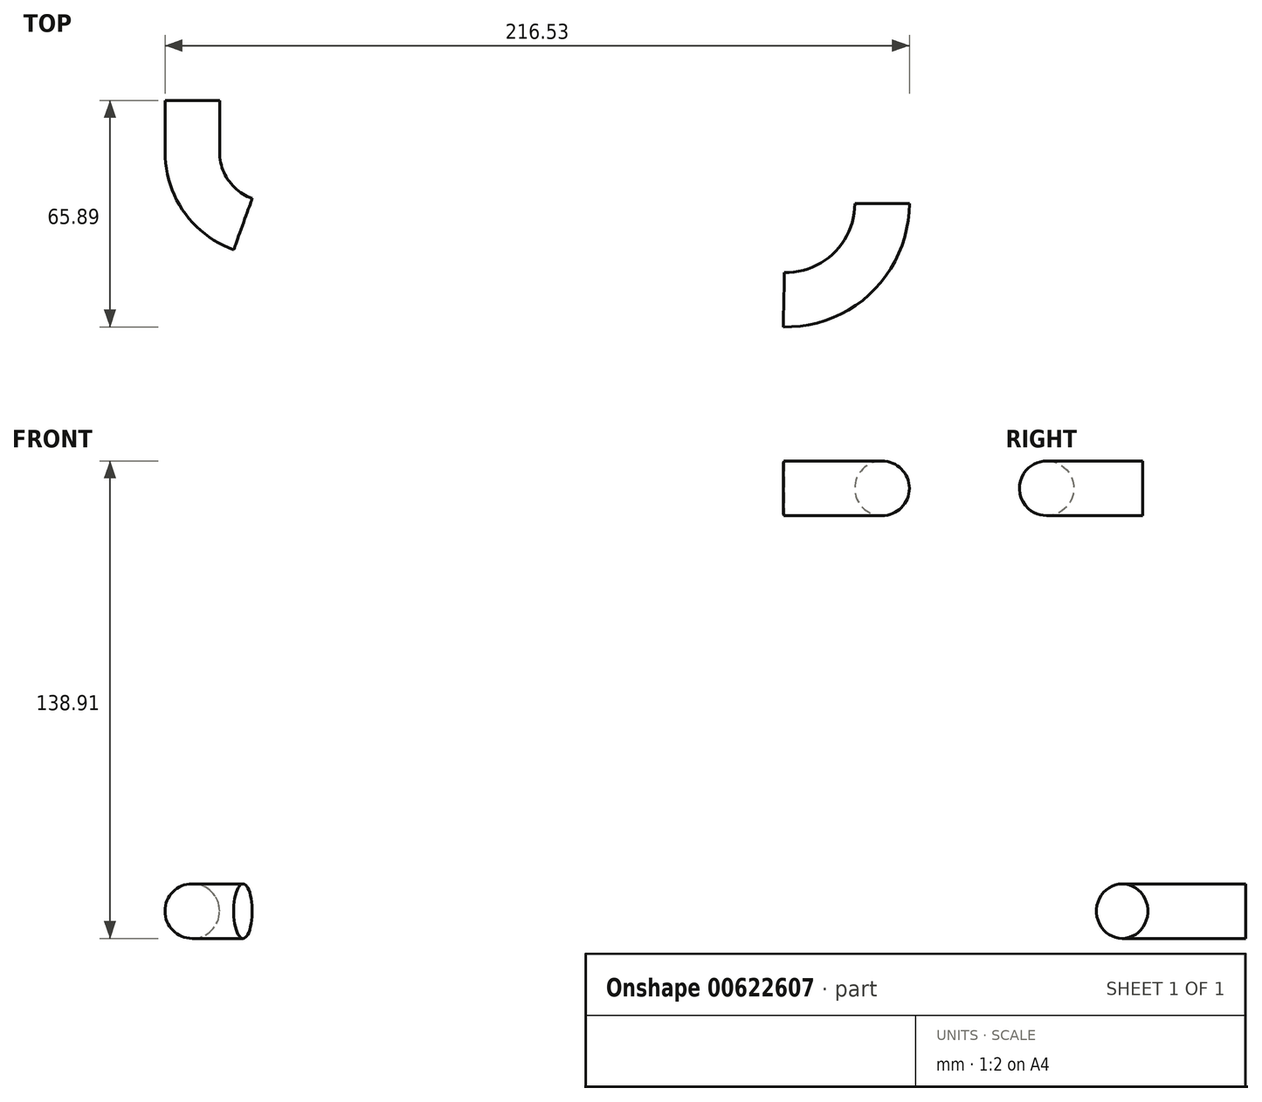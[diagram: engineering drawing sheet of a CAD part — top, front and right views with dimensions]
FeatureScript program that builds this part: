
annotation { "Feature Type Name" : "Feature", "Feature Type Description" : "" }
export const myFeature = defineFeature(function(context is Context, id is Id, definition is map)
    precondition{}
    {
        {
            var Q0;
            Q0=qCreatedBy(makeId("Front.planeOp"),FACE);
            var sketch = newSketch(context, id + "F0", { "sketchPlane" : qUnion([Q0])});
            skLineSegment(sketch, "E0", {"start": v(-200.65, -116.68) * mm, "end": v(-200.65, -136.52) * mm, "construction": true});
            skLineSegment(sketch, "E1", {"start": v(-200.65, -136.53) * mm, "end": v(0, -136.52) * mm, "construction": true});
            skLineSegment(sketch, "E2", {"start": v(0, -136.52) * mm, "end": v(0, 0) * mm, "construction": true});
            skCircle(sketch, "E3", {"center": v(-200.65, -116.68) * mm, "radius": 7.94 * mm});
            skLineSegment(sketch, "E4", {"start": v(0, 0) * mm, "end": v(0, 6.35) * mm, "construction": true});
            skSolve(sketch);
        }
        {
            var Q0;
            Q0=qCreatedBy(makeId("Front.planeOp"),FACE);
            cPlane(context, id + "F1", {"entities" : qUnion([Q0]), "cplaneType" : CPlaneType.OFFSET, "offset" : 30 * mm, "width" : 152.4 * mm, "height" : 152.4 * mm});
        }
        {
            var Q0;
            Q0=qCreatedBy(id+"F1.planeOp",FACE);
            var sketch = newSketch(context, id + "F2", { "sketchPlane" : qUnion([Q0])});
            skLineSegment(sketch, "E5", {"start": v(0, 0) * mm, "end": v(0, -136.53) * mm, "construction": true});
            skLineSegment(sketch, "E6", {"start": v(0, -136.53) * mm, "end": v(-200.65, -136.53) * mm, "construction": true});
            skLineSegment(sketch, "E7", {"start": v(-200.65, -136.53) * mm, "end": v(-200.65, -116.68) * mm, "construction": true});
            skLineSegment(sketch, "E8", {"start": v(0, 0) * mm, "end": v(0, 6.35) * mm, "construction": true});
            skCircle(sketch, "E9", {"center": v(0, 6.35) * mm, "radius": 7.94 * mm});
            skSolve(sketch);
        }
        {
            var Q0;
            Q0=qCreatedBy(makeId("Top.planeOp"),FACE);
            cPlane(context, id + "F3", {"entities" : qUnion([Q0]), "cplaneType" : CPlaneType.OFFSET, "offset" : 116.68 * mm, "oppositeDirection" : true, "width" : 152.4 * mm, "height" : 152.4 * mm});
        }
        {
            var Q0;
            Q0=qCreatedBy(id+"F3.planeOp",FACE);
            var sketch = newSketch(context, id + "F4", { "sketchPlane" : qUnion([Q0])});
            skLineSegment(sketch, "E10", {"start": v(0, 0) * mm, "end": v(-200.65, 0) * mm, "construction": true});
            skLineSegment(sketch, "E11", {"start": v(-200.65, 0) * mm, "end": v(-200.65, -15) * mm});
            skLineSegment(sketch, "E12", {"start": v(-184.78, -15) * mm, "end": v(-184.78, -30) * mm, "construction": true});
            skLineSegment(sketch, "E13", {"start": v(-184.78, -22.5) * mm, "end": v(-199.35, -22.5) * mm, "construction": true});
            skLineSegment(sketch, "E14", {"start": v(-184.78, -30) * mm, "end": v(-184.78, -36.35) * mm, "construction": true});
            skArc(sketch, "E15", {"start": v(-200.65, -15) * mm, "mid": v(-196.6, -27.82) * mm, "end": v(-185.92, -35.98) * mm});
            skLineSegment(sketch, "E16", {"start": v(-183.76, -36.35) * mm, "end": v(-100.33, -36.35) * mm});
            skPoint(sketch, "E17.visualSharp", {"position": v(-184.78, -36.35) * mm});
            skArc(sketch, "E17.filletArc", {"start": v(-185.92, -35.98) * mm, "mid": v(-184.86, -36.26) * mm, "end": v(-183.76, -36.35) * mm});
            skSolve(sketch);
        }
        {
            var Q0;
            Q0=makeQuery(id+"F0.imprint","IMPRINT",FACE,{"disambiguationData":[TD([[makeQuery(id+"F0.imprint","IMPRINT",EDGE,{"derivedFrom":sQuery(id+"F0.wireOp",EDGE,"E3")}),1.0]])]});
            var Q1;
            Q1=sQuery(id+"F4.wireOp",EDGE,"E11");
            var Q2;
            Q2=sQuery(id+"F4.wireOp",EDGE,"E15");
            sweep(context, id + "F5", {"profiles" : qUnion([Q0]), "path" : qUnion([Q1, Q2])});
        }
        {
            var Q0;
            Q0=qCreatedBy(makeId("Top.planeOp"),FACE);
            cPlane(context, id + "F6", {"entities" : qUnion([Q0]), "cplaneType" : CPlaneType.OFFSET, "offset" : 6.35 * mm, "width" : 152.4 * mm, "height" : 152.4 * mm});
        }
        {
            var Q0;
            Q0=qCreatedBy(id+"F6.planeOp",FACE);
            var sketch = newSketch(context, id + "F7", { "sketchPlane" : qUnion([Q0])});
            skLineSegment(sketch, "E18", {"start": v(0, 0) * mm, "end": v(0, -30) * mm, "construction": true});
            skLineSegment(sketch, "E19", {"start": v(0, -42.7) * mm, "end": v(0, -30) * mm, "construction": true});
            skLineSegment(sketch, "E20", {"start": v(0, -42.7) * mm, "end": v(-60.4, -42.7) * mm, "construction": true});
            skLineSegment(sketch, "E21", {"start": v(-28.57, -42.7) * mm, "end": v(-28.57, -4.7) * mm, "construction": true});
            skLineSegment(sketch, "E22", {"start": v(-28.57, -42.7) * mm, "end": v(-28.57, -57.94) * mm, "construction": true});
            skLineSegment(sketch, "E23", {"start": v(0, -30) * mm, "end": v(0, -42.7) * mm});
            skArc(sketch, "E24", {"start": v(-28.57, -57.94) * mm, "mid": v(-8.4, -49.99) * mm, "end": v(0, -30) * mm});
            skSolve(sketch);
        }
        {
            var Q0;
            Q0=makeQuery(id+"F2.imprint","IMPRINT",FACE,{"disambiguationData":[TD([[makeQuery(id+"F2.imprint","IMPRINT",EDGE,{"derivedFrom":sQuery(id+"F2.wireOp",EDGE,"E9")}),1.0]])]});
            var Q1;
            Q1=sQuery(id+"F7.wireOp",EDGE,"E24");
            sweep(context, id + "F8", {"profiles" : qUnion([Q0]), "path" : qUnion([Q1])});
        }
    });
